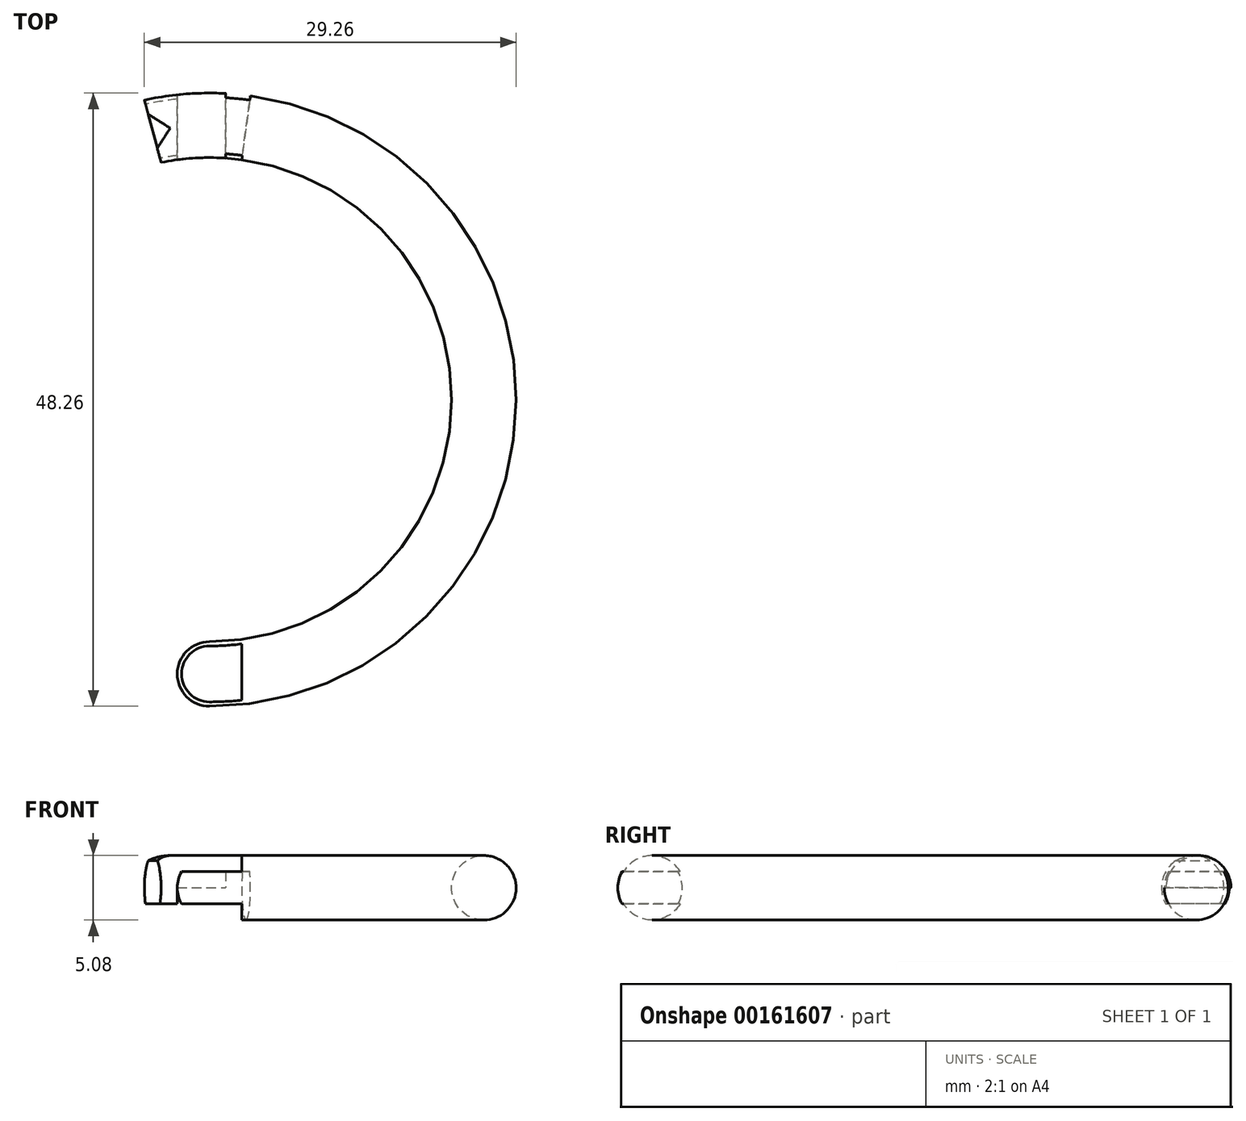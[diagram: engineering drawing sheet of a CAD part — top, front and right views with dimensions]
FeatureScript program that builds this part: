
annotation { "Feature Type Name" : "Feature", "Feature Type Description" : "" }
export const myFeature = defineFeature(function(context is Context, id is Id, definition is map)
    precondition{}
    {
        {
            var Q0;
            Q0=qCreatedBy(makeId("Top.planeOp"),FACE);
            var sketch = newSketch(context, id + "F0", { "sketchPlane" : qUnion([Q0])});
            skArc(sketch, "E0", {"start": v(0, -19.05) * mm, "mid": v(18.89, 2.49) * mm, "end": v(-4.93, 18.4) * mm});
            skArc(sketch, "E1", {"start": v(0, -24.13) * mm, "mid": v(23.92, 3.15) * mm, "end": v(-6.25, 23.3) * mm});
            skArc(sketch, "E2", {"start": v(0, -19.05) * mm, "mid": v(-2.54, -21.59) * mm, "end": v(0, -24.13) * mm});
            skLineSegment(sketch, "E3", {"start": v(-6.25, 23.3) * mm, "end": v(0, 0) * mm});
            skLineSegment(sketch, "E4", {"start": v(0, 0) * mm, "end": v(0, 24.13) * mm, "construction": true});
            skSolve(sketch);
        }
        {
            var Q0;
            Q0 = qSketchRegion(id + "F0", true);
            extrude(context, id + "F1", {"entities" : qUnion([Q0]), "depth" : 5.08 * mm});
        }
        {
            var Q0;
            Q0=makeQuery(id+"F1.opExtrude","CAP_FACE",FACE,{"disambiguationData":[OSD([sQuery(id+"F0.wireOp",EDGE,"E0"),sQuery(id+"F0.wireOp",EDGE,"E1"),sQuery(id+"F0.wireOp",EDGE,"rdsI8oK9-sf5B-igfl-71Gm-wbMa6m2B4cqI"),sQuery(id+"F0.wireOp",EDGE,"E2")])],"isStart":false});
            var Q1;
            Q1=makeQuery(id+"F1.opExtrude","CAP_FACE",FACE,{"disambiguationData":[OSD([sQuery(id+"F0.wireOp",EDGE,"E0"),sQuery(id+"F0.wireOp",EDGE,"E1"),sQuery(id+"F0.wireOp",EDGE,"rdsI8oK9-sf5B-igfl-71Gm-wbMa6m2B4cqI"),sQuery(id+"F0.wireOp",EDGE,"E2")])],"isStart":true});
            fillet(context, id + "F2", {"entities" : qUnion([Q0, Q1]), "radius" : 2.54 * mm, "tangentPropagation" : true, "allowEdgeOverflow" : false});
        }
        {
            var Q0;
            Q0=qCreatedBy(makeId("Top.planeOp"),FACE);
            cPlane(context, id + "F3", {"entities" : qUnion([Q0]), "cplaneType" : CPlaneType.OFFSET, "offset" : 2.54 * mm, "width" : 152.4 * mm, "height" : 152.4 * mm});
        }
        {
            var Q0;
            Q0=qCreatedBy(id+"F3.planeOp",FACE);
            var sketch = newSketch(context, id + "F4", { "sketchPlane" : qUnion([Q0])});
            skLineSegment(sketch, "E5.bottom", {"start": v(2.54, 17.78) * mm, "end": v(-2.54, 17.78) * mm});
            skLineSegment(sketch, "E5.top", {"start": v(2.54, 25.4) * mm, "end": v(-2.54, 25.4) * mm});
            skLineSegment(sketch, "E5.left", {"start": v(2.54, 17.78) * mm, "end": v(2.54, 25.4) * mm});
            skLineSegment(sketch, "E5.right", {"start": v(-2.54, 17.78) * mm, "end": v(-2.54, 25.4) * mm});
            skPoint(sketch, "E5.middle", {"position": v(0, 21.59) * mm});
            skSolve(sketch);
        }
        {
            var Q0;
            Q0=makeQuery(id+"F4.imprint","IMPRINT",FACE,{"disambiguationData":[TD([[makeQuery(id+"F4.imprint","IMPRINT",EDGE,{"derivedFrom":sQuery(id+"F4.wireOp",EDGE,"E5.bottom")}),-1.0]])]});
            extrude(context, id + "F5", {"entities" : qUnion([Q0]), "operationType" : NewBodyOperationType.REMOVE, "oppositeDirection" : true, "depth" : 25.4 * mm});
        }
        {
            var Q0;
            Q0=qCreatedBy(id+"F3.planeOp",FACE);
            cPlane(context, id + "F6", {"entities" : qUnion([Q0]), "cplaneType" : CPlaneType.OFFSET, "offset" : 1.27 * mm, "width" : 152.4 * mm, "height" : 152.4 * mm});
        }
        {
            var Q0;
            Q0=qCreatedBy(id+"F3.planeOp",FACE);
            cPlane(context, id + "F7", {"entities" : qUnion([Q0]), "cplaneType" : CPlaneType.OFFSET, "offset" : 1.27 * mm, "oppositeDirection" : true, "width" : 152.4 * mm, "height" : 152.4 * mm});
        }
        {
            var Q0;
            Q0=qCreatedBy(id+"F7.planeOp",FACE);
            var sketch = newSketch(context, id + "F8", { "sketchPlane" : qUnion([Q0])});
            skLineSegment(sketch, "E6.bottom", {"start": v(-2.54, -25.4) * mm, "end": v(2.54, -25.4) * mm});
            skLineSegment(sketch, "E6.top", {"start": v(-2.54, -17.78) * mm, "end": v(2.54, -17.78) * mm});
            skLineSegment(sketch, "E6.left", {"start": v(-2.54, -25.4) * mm, "end": v(-2.54, -17.78) * mm});
            skLineSegment(sketch, "E6.right", {"start": v(2.54, -25.4) * mm, "end": v(2.54, -17.78) * mm});
            skPoint(sketch, "E6.middle", {"position": v(0, -21.59) * mm});
            skSolve(sketch);
        }
        {
            var Q0;
            Q0=makeQuery(id+"F8.imprint","IMPRINT",FACE,{"disambiguationData":[TD([[makeQuery(id+"F8.imprint","IMPRINT",EDGE,{"derivedFrom":sQuery(id+"F8.wireOp",EDGE,"E6.bottom")}),1.0]])]});
            extrude(context, id + "F9", {"entities" : qUnion([Q0]), "operationType" : NewBodyOperationType.REMOVE, "oppositeDirection" : true, "depth" : 25.4 * mm});
        }
        {
            var Q0;
            Q0=qCreatedBy(id+"F6.planeOp",FACE);
            var sketch = newSketch(context, id + "F10", { "sketchPlane" : qUnion([Q0])});
            skLineSegment(sketch, "E7.bottom", {"start": v(2.54, -25.4) * mm, "end": v(-2.54, -25.4) * mm});
            skLineSegment(sketch, "E7.top", {"start": v(2.54, -17.78) * mm, "end": v(-2.54, -17.78) * mm});
            skLineSegment(sketch, "E7.left", {"start": v(2.54, -25.4) * mm, "end": v(2.54, -17.78) * mm});
            skLineSegment(sketch, "E7.right", {"start": v(-2.54, -25.4) * mm, "end": v(-2.54, -17.78) * mm});
            skPoint(sketch, "E7.middle", {"position": v(0, -21.59) * mm});
            skSolve(sketch);
        }
        {
            var Q0;
            Q0 = qSketchRegion(id + "F10", true);
            extrude(context, id + "F11", {"entities" : qUnion([Q0]), "operationType" : NewBodyOperationType.REMOVE, "depth" : 25.4 * mm});
        }
        {
            var Q0;
            Q0=qCreatedBy(makeId("Top.planeOp"),FACE);
            var sketch = newSketch(context, id + "F12", { "sketchPlane" : qUnion([Q0])});
            skArc(sketch, "E8", {"start": v(-2.54, 24) * mm, "mid": v(-4.4, 23.72) * mm, "end": v(-6.25, 23.3) * mm});
            skArc(sketch, "E9", {"start": v(-2.54, 18.88) * mm, "mid": v(-3.74, 18.68) * mm, "end": v(-4.93, 18.4) * mm});
            skLineSegment(sketch, "E10", {"start": v(-2.54, 24) * mm, "end": v(-2.54, 18.88) * mm});
            skLineSegment(sketch, "E11", {"start": v(-6.25, 23.3) * mm, "end": v(-4.93, 18.4) * mm});
            skSolve(sketch);
        }
        {
            var Q0;
            Q0 = qSketchRegion(id + "F12", true);
            extrude(context, id + "F13", {"entities" : qUnion([Q0]), "operationType" : NewBodyOperationType.REMOVE, "depth" : 1.27 * mm});
        }
        {
            var Q0;
            Q0=qCreatedBy(makeId("Top.planeOp"),FACE);
            var sketch = newSketch(context, id + "F14", { "sketchPlane" : qUnion([Q0])});
            skArc(sketch, "E12", {"start": v(-5.13, 23.58) * mm, "mid": v(-5.69, 23.45) * mm, "end": v(-6.25, 23.3) * mm});
            skArc(sketch, "E13", {"start": v(-3.81, 18.67) * mm, "mid": v(-4.37, 18.54) * mm, "end": v(-4.93, 18.4) * mm});
            skLineSegment(sketch, "E14", {"start": v(-6.25, 23.3) * mm, "end": v(-4.93, 18.4) * mm});
            skLineSegment(sketch, "E15", {"start": v(-3.8, 18.67) * mm, "end": v(-5.13, 23.58) * mm});
            skSolve(sketch);
        }
        {
            var Q0;
            Q0 = qSketchRegion(id + "F14", true);
            extrude(context, id + "F15", {"entities" : qUnion([Q0]), "operationType" : NewBodyOperationType.REMOVE, "depth" : 25.4 * mm});
        }
        {
            var Q0;
            Q0=makeQuery(id+"F5.boolean.opBoolean","COPY",FACE,{"derivedFrom":makeQuery(id+"F5.opExtrude","CAP_FACE",FACE,{"disambiguationData":[OSD([sQuery(id+"F4.wireOp",EDGE,"E5.bottom"),sQuery(id+"F4.wireOp",EDGE,"E5.top"),sQuery(id+"F4.wireOp",EDGE,"E5.left"),sQuery(id+"F4.wireOp",EDGE,"E5.right")])],"isStart":true})});
            var sketch = newSketch(context, id + "F16", { "sketchPlane" : qUnion([Q0])});
            skLineSegment(sketch, "E16", {"start": v(1.27, -19) * mm, "end": v(1.27, -24.1) * mm});
            skArc(sketch, "E17", {"start": v(1.27, -24.1) * mm, "mid": v(2.25, -24.03) * mm, "end": v(3.22, -23.91) * mm});
            skArc(sketch, "E18", {"start": v(1.27, -19) * mm, "mid": v(1.9, -18.95) * mm, "end": v(2.54, -18.88) * mm});
            skLineSegment(sketch, "E19", {"start": v(3.22, -23.91) * mm, "end": v(2.54, -18.88) * mm});
            skLineSegment(sketch, "E20", {"start": v(4.89, -23.69) * mm, "end": v(1.55, -24.14) * mm, "construction": true});
            skSolve(sketch);
        }
        {
            var Q0;
            Q0 = qSketchRegion(id + "F16", true);
            extrude(context, id + "F17", {"entities" : qUnion([Q0]), "operationType" : NewBodyOperationType.REMOVE, "oppositeDirection" : true, "depth" : 1.27 * mm, "hasSecondDirection" : true, "secondDirectionOppositeDirection" : false, "secondDirectionDepth" : 25.4 * mm});
        }
        {
            var Q0;
            Q0 = qSketchRegion(id + "F14", true);
            extrude(context, id + "F18", {"entities" : qUnion([Q0]), "operationType" : NewBodyOperationType.REMOVE, "depth" : 25.4 * mm});
        }
    });
